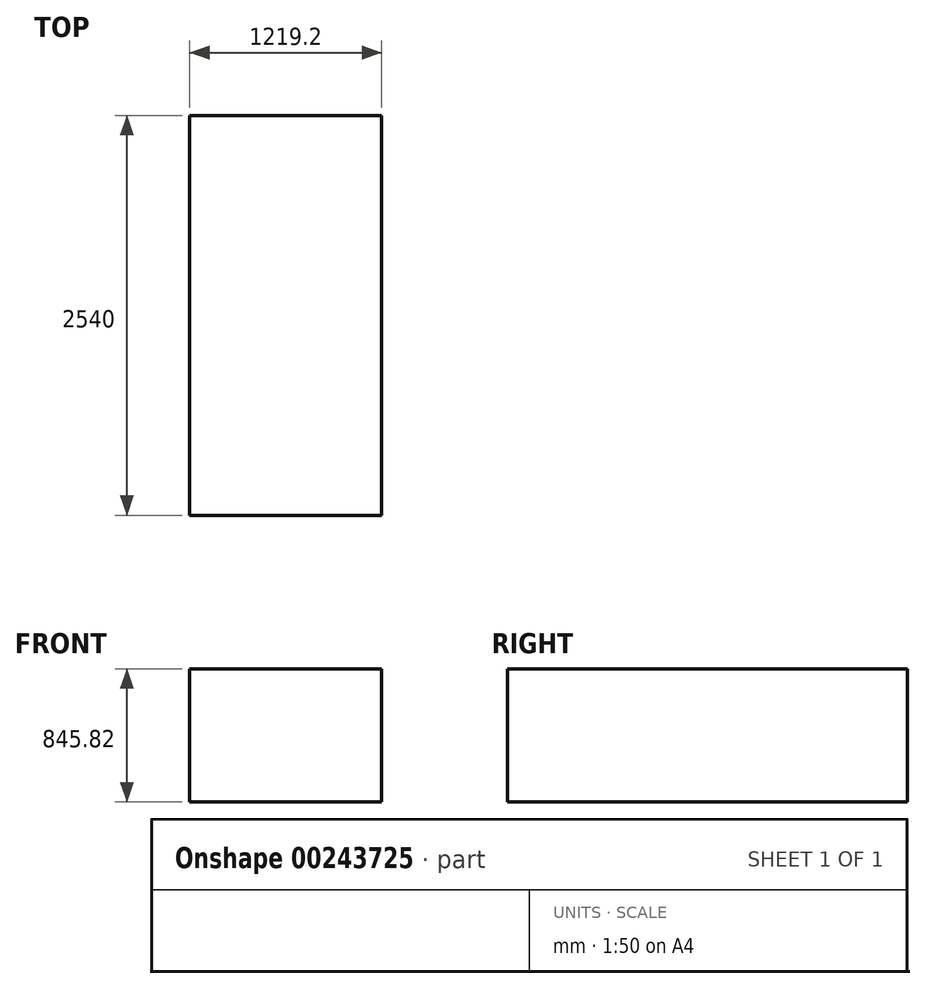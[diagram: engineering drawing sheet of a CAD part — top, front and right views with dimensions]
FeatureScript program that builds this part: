
annotation { "Feature Type Name" : "Feature", "Feature Type Description" : "" }
export const myFeature = defineFeature(function(context is Context, id is Id, definition is map)
    precondition{}
    {
        {
            var Q0;
            Q0=qCreatedBy(makeId("Top.planeOp"),FACE);
            var sketch = newSketch(context, id + "F0", { "sketchPlane" : qUnion([Q0])});
            skLineSegment(sketch, "E0.bottom", {"start": v(-612.32, 1272.52) * mm, "end": v(606.88, 1272.52) * mm});
            skLineSegment(sketch, "E0.top", {"start": v(-612.32, -1267.48) * mm, "end": v(606.88, -1267.48) * mm});
            skLineSegment(sketch, "E0.left", {"start": v(-612.32, 1272.52) * mm, "end": v(-612.32, -1267.48) * mm});
            skLineSegment(sketch, "E0.right", {"start": v(606.88, 1272.52) * mm, "end": v(606.88, -1267.48) * mm});
            skSolve(sketch);
        }
        {
            var Q0;
            Q0=makeQuery(id+"F0.imprint","IMPRINT",FACE,{"disambiguationData":[TD([[makeQuery(id+"F0.imprint","IMPRINT",EDGE,{"derivedFrom":sQuery(id+"F0.wireOp",EDGE,"E0.bottom")}),-1.0]])]});
            extrude(context, id + "F1", {"entities" : qUnion([Q0]), "depth" : 845.82 * mm});
        }
    });
